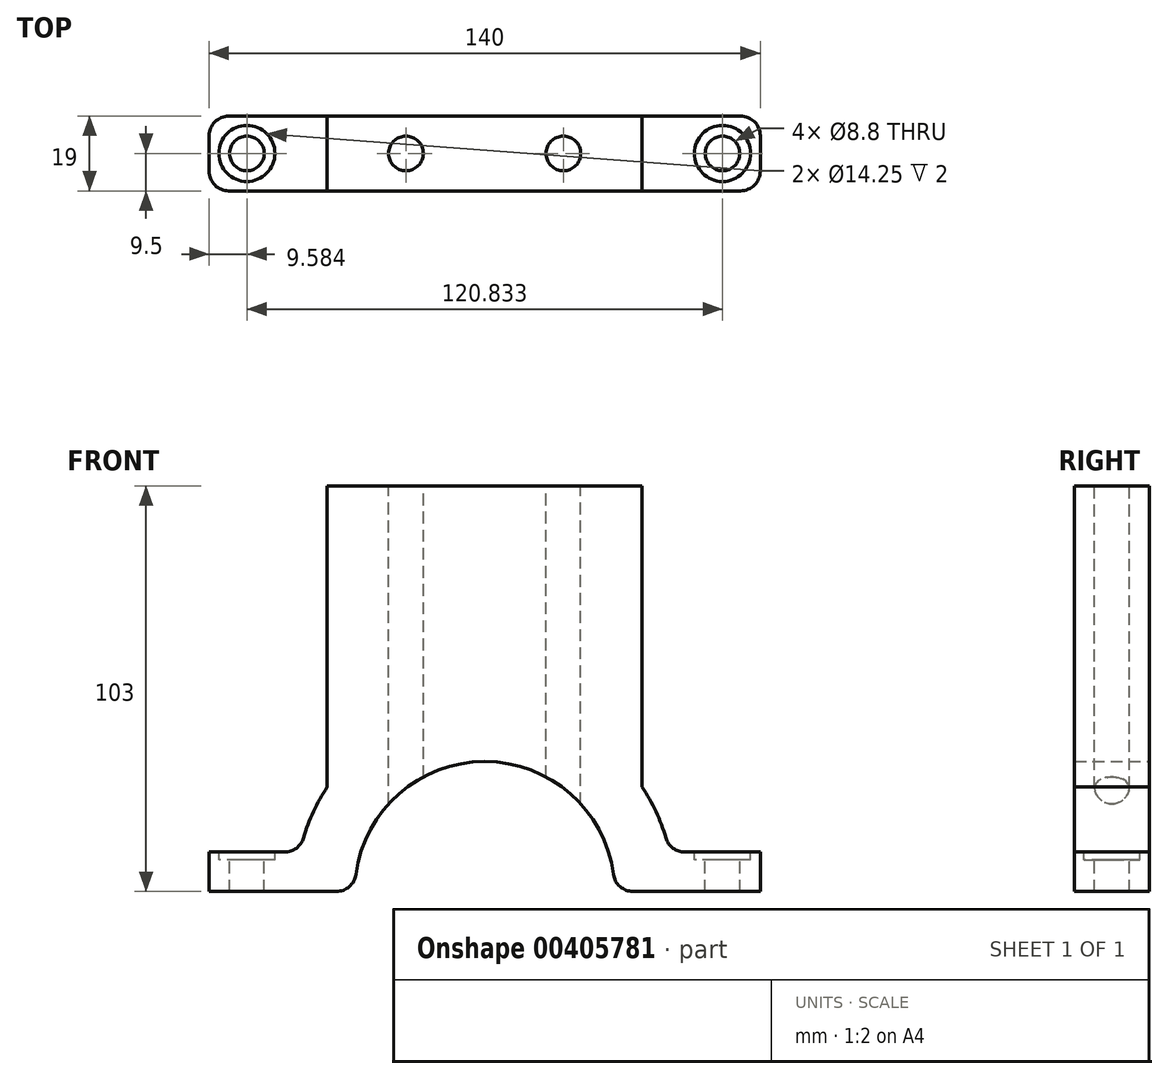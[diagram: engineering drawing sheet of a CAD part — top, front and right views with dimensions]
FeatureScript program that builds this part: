
annotation { "Feature Type Name" : "Feature", "Feature Type Description" : "" }
export const myFeature = defineFeature(function(context is Context, id is Id, definition is map)
    precondition{}
    {
        {
            var Q0;
            Q0=qCreatedBy(makeId("Front.planeOp"),FACE);
            var sketch = newSketch(context, id + "F0", { "sketchPlane" : qUnion([Q0])});
            skArc(sketch, "E0", {"start": v(32.71, 4.34) * mm, "mid": v(0, 33) * mm, "end": v(-32.71, 4.34) * mm});
            skArc(sketch, "E1.0", {"start": v(46.04, 13.58) * mm, "mid": v(43.5, 20.28) * mm, "end": v(40, 26.53) * mm});
            skLineSegment(sketch, "E2", {"start": v(37.67, 0) * mm, "end": v(70, 0) * mm});
            skLineSegment(sketch, "E3", {"start": v(-37.67, 0) * mm, "end": v(-70, 0) * mm});
            skLineSegment(sketch, "E4.0", {"start": v(50.83, 10) * mm, "end": v(70, 10) * mm});
            skLineSegment(sketch, "E5.0", {"start": v(-50.83, 10) * mm, "end": v(-70, 10) * mm});
            skLineSegment(sketch, "E6", {"start": v(-70, 10) * mm, "end": v(-70, 0) * mm});
            skLineSegment(sketch, "E7", {"start": v(70, 10) * mm, "end": v(70, 0) * mm});
            skPoint(sketch, "E8.visualSharp", {"position": v(46.95, 10) * mm});
            skArc(sketch, "E8.filletArc", {"start": v(46.04, 13.58) * mm, "mid": v(47.84, 11) * mm, "end": v(50.83, 10) * mm});
            skPoint(sketch, "E9.visualSharp", {"position": v(-46.95, 10) * mm});
            skArc(sketch, "E9.filletArc", {"start": v(-50.83, 10) * mm, "mid": v(-47.84, 11) * mm, "end": v(-46.04, 13.58) * mm});
            skPoint(sketch, "E10.visualSharp", {"position": v(-33, 0) * mm});
            skArc(sketch, "E10.filletArc", {"start": v(-37.67, 0) * mm, "mid": v(-34.37, 1.24) * mm, "end": v(-32.71, 4.34) * mm});
            skPoint(sketch, "E11.visualSharp", {"position": v(33, 0) * mm});
            skArc(sketch, "E11.filletArc", {"start": v(32.71, 4.34) * mm, "mid": v(34.37, 1.24) * mm, "end": v(37.67, 0) * mm});
            skPoint(sketch, "E12.endSnap0", {"position": v(0, 48) * mm});
            skLineSegment(sketch, "E13", {"start": v(0, 103) * mm, "end": v(-40, 103) * mm});
            skLineSegment(sketch, "E14", {"start": v(-40, 103) * mm, "end": v(-40, 26.53) * mm});
            skLineSegment(sketch, "E15.MirrorCS", {"start": v(0, 103) * mm, "end": v(40, 103) * mm});
            skLineSegment(sketch, "E16.MirrorCS", {"start": v(40, 103) * mm, "end": v(40, 26.53) * mm});
            skArc(sketch, "E17.trimOffspring", {"start": v(-40, 26.53) * mm, "mid": v(-43.5, 20.28) * mm, "end": v(-46.04, 13.58) * mm});
            skSolve(sketch);
        }
        {
            var Q0;
            Q0=makeQuery(id+"F0.imprint","IMPRINT",FACE,{"disambiguationData":[TD([[makeQuery(id+"F0.imprint","IMPRINT",EDGE,{"derivedFrom":sQuery(id+"F0.wireOp",EDGE,"E0")}),-1.0]])]});
            extrude(context, id + "F1", {"entities" : qUnion([Q0]), "depth" : 19 * mm});
        }
        {
            var Q0;
            Q0=makeQuery(id+"F1.opExtrude","SWEPT_FACE",FACE,{"disambiguationData":[OSD([sQuery(id+"F0.wireOp",EDGE,"E4.0")])]});
            var sketch = newSketch(context, id + "F2", { "sketchPlane" : qUnion([Q0])});
            skLineSegment(sketch, "E18", {"start": v(50.83, 0) * mm, "end": v(70, -19) * mm});
            skLineSegment(sketch, "E19", {"start": v(70, 0) * mm, "end": v(50.83, -19) * mm});
            skCircle(sketch, "E20", {"center": v(60.42, -9.5) * mm, "radius": 4.25 * mm});
            skSolve(sketch);
        }
        {
            var Q0;
            Q0=sQuery(id+"F2.wireOp",VERTEX,"E20.center");
            var Q1;
            Q1=makeQuery(id+"F1.opExtrude","SWEPT_BODY",BODY,{"disambiguationData":[OSD([sQuery(id+"F0.wireOp",EDGE,"E0"),sQuery(id+"F0.wireOp",EDGE,"E1.0"),sQuery(id+"F0.wireOp",EDGE,"E2"),sQuery(id+"F0.wireOp",EDGE,"E3"),sQuery(id+"F0.wireOp",EDGE,"E4.0"),sQuery(id+"F0.wireOp",EDGE,"E5.0"),sQuery(id+"F0.wireOp",EDGE,"E6"),sQuery(id+"F0.wireOp",EDGE,"E7"),sQuery(id+"F0.wireOp",EDGE,"E8.filletArc"),sQuery(id+"F0.wireOp",EDGE,"E9.filletArc"),sQuery(id+"F0.wireOp",EDGE,"E10.filletArc"),sQuery(id+"F0.wireOp",EDGE,"E11.filletArc")])]});
            hole(context, id + "F3", {"style" : HoleStyle.C_BORE, "endStyle" : HoleEndStyle.THROUGH, "holeDiameter" : 8.8 * mm, "cBoreDiameter" : 14.25 * mm, "cBoreDepth" : 2 * mm, "tappedDepth" : 12 * mm, "tapClearance" : 3, "locations" : qUnion([Q0]), "scope" : qUnion([Q1])});
        }
        {
            var Q0;
            Q0=makeQuery(id+"F1.opExtrude","CAP_EDGE",EDGE,{"disambiguationData":[OSD([sQuery(id+"F0.wireOp",EDGE,"E7")])],"isStart":false});
            var Q1;
            Q1=makeQuery(id+"F1.opExtrude","CAP_EDGE",EDGE,{"disambiguationData":[OSD([sQuery(id+"F0.wireOp",EDGE,"E7")])],"isStart":true});
            fillet(context, id + "F4", {"entities" : qUnion([Q0, Q1]), "radius" : 5 * mm, "tangentPropagation" : true, "allowEdgeOverflow" : false});
        }
        {
            var Q0;
            Q0=makeQuery(id+"F1.opExtrude","SWEPT_FACE",FACE,{"disambiguationData":[OSD([sQuery(id+"F0.wireOp",EDGE,"E5.0")])]});
            var sketch = newSketch(context, id + "F5", { "sketchPlane" : qUnion([Q0])});
            skLineSegment(sketch, "E21", {"start": v(-50.83, -19) * mm, "end": v(-70, 0) * mm});
            skLineSegment(sketch, "E22", {"start": v(-70, 0) * mm, "end": v(-60.42, -9.5) * mm});
            skLineSegment(sketch, "E23", {"start": v(-60.42, -9.5) * mm, "end": v(-70, -19) * mm});
            skSolve(sketch);
        }
        {
            var Q0;
            Q0=sQuery(id+"F5.wireOp",VERTEX,"E23.start");
            var Q1;
            Q1=makeQuery(id+"F1.opExtrude","SWEPT_BODY",BODY,{"disambiguationData":[OSD([sQuery(id+"F0.wireOp",EDGE,"E0"),sQuery(id+"F0.wireOp",EDGE,"E1.0"),sQuery(id+"F0.wireOp",EDGE,"E2"),sQuery(id+"F0.wireOp",EDGE,"E3"),sQuery(id+"F0.wireOp",EDGE,"E4.0"),sQuery(id+"F0.wireOp",EDGE,"E5.0"),sQuery(id+"F0.wireOp",EDGE,"E6"),sQuery(id+"F0.wireOp",EDGE,"E7"),sQuery(id+"F0.wireOp",EDGE,"E8.filletArc"),sQuery(id+"F0.wireOp",EDGE,"E9.filletArc"),sQuery(id+"F0.wireOp",EDGE,"E10.filletArc"),sQuery(id+"F0.wireOp",EDGE,"E11.filletArc")])]});
            hole(context, id + "F6", {"style" : HoleStyle.C_BORE, "endStyle" : HoleEndStyle.THROUGH, "holeDiameter" : 8.8 * mm, "cBoreDiameter" : 14.25 * mm, "cBoreDepth" : 2 * mm, "tappedDepth" : 12 * mm, "tapClearance" : 3, "locations" : qUnion([Q0]), "scope" : qUnion([Q1])});
        }
        {
            var Q0;
            Q0=makeQuery(id+"F1.opExtrude","CAP_EDGE",EDGE,{"disambiguationData":[OSD([sQuery(id+"F0.wireOp",EDGE,"E6")])],"isStart":false});
            var Q1;
            Q1=makeQuery(id+"F1.opExtrude","CAP_EDGE",EDGE,{"disambiguationData":[OSD([sQuery(id+"F0.wireOp",EDGE,"E6")])],"isStart":true});
            fillet(context, id + "F7", {"entities" : qUnion([Q0, Q1]), "radius" : 5 * mm, "tangentPropagation" : true, "allowEdgeOverflow" : false});
        }
        {
            var Q0;
            Q0=makeQuery(id+"F1.opExtrude","SWEPT_FACE",FACE,{"disambiguationData":[OSD([sQuery(id+"F0.wireOp",EDGE,"E13"),sQuery(id+"F0.wireOp",EDGE,"E15.MirrorCS")])]});
            var sketch = newSketch(context, id + "F8", { "sketchPlane" : qUnion([Q0])});
            skLineSegment(sketch, "E24", {"start": v(40, -9.5) * mm, "end": v(-40, -9.5) * mm});
            skLineSegment(sketch, "E25", {"start": v(0, 0) * mm, "end": v(0, -19) * mm});
            skLineSegment(sketch, "E26.0", {"start": v(-20, 0) * mm, "end": v(-20, -19) * mm});
            skLineSegment(sketch, "E27.0", {"start": v(20, 0) * mm, "end": v(20, -19) * mm});
            skCircle(sketch, "E28", {"center": v(20, -9.5) * mm, "radius": 7.12 * mm});
            skCircle(sketch, "E29", {"center": v(-20, -9.5) * mm, "radius": 6.6 * mm});
            skSolve(sketch);
        }
        {
            var Q0;
            Q0=sQuery(id+"F8.wireOp",VERTEX,"E28.center");
            var Q1;
            Q1=sQuery(id+"F8.wireOp",VERTEX,"E29.center");
            var Q2;
            Q2=makeQuery(id+"F1.opExtrude","SWEPT_BODY",BODY,{"disambiguationData":[OSD([sQuery(id+"F0.wireOp",EDGE,"E0"),sQuery(id+"F0.wireOp",EDGE,"E1.0"),sQuery(id+"F0.wireOp",EDGE,"E2"),sQuery(id+"F0.wireOp",EDGE,"E3"),sQuery(id+"F0.wireOp",EDGE,"E4.0"),sQuery(id+"F0.wireOp",EDGE,"E5.0"),sQuery(id+"F0.wireOp",EDGE,"E6"),sQuery(id+"F0.wireOp",EDGE,"E7"),sQuery(id+"F0.wireOp",EDGE,"E8.filletArc"),sQuery(id+"F0.wireOp",EDGE,"E9.filletArc"),sQuery(id+"F0.wireOp",EDGE,"E10.filletArc"),sQuery(id+"F0.wireOp",EDGE,"E11.filletArc"),sQuery(id+"F0.wireOp",EDGE,"E13"),sQuery(id+"F0.wireOp",EDGE,"E14"),sQuery(id+"F0.wireOp",EDGE,"E15.MirrorCS"),sQuery(id+"F0.wireOp",EDGE,"E16.MirrorCS"),sQuery(id+"F0.wireOp",EDGE,"E17.trimOffspring")])]});
            hole(context, id + "F9", {"style" : HoleStyle.SIMPLE, "endStyle" : HoleEndStyle.THROUGH, "standardTappedOrClearance" : lookupTablePath({ "standard" : "ISO", "fit" : "Normal", "size" : "M8", "type" : "Clearance" }), "standardBlindInLast" : lookupTablePath({ "fit" : "Standard", "standard" : "ISO", "size" : "M8", "type" : "Clearance" }), "holeDiameter" : 8.8 * mm, "tappedDepth" : 12 * mm, "tapClearance" : 3, "locations" : qUnion([Q0, Q1]), "scope" : qUnion([Q2])});
        }
    });
